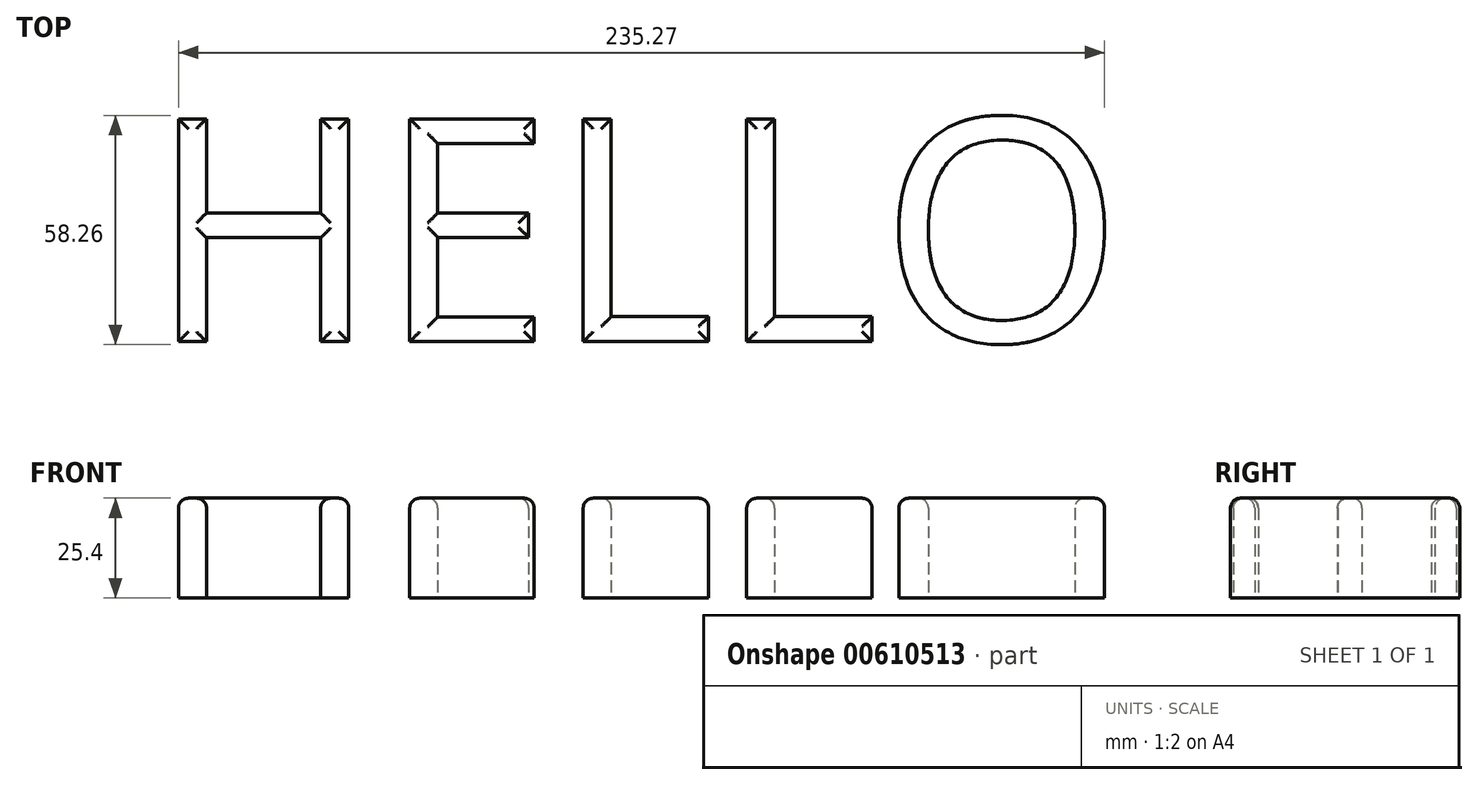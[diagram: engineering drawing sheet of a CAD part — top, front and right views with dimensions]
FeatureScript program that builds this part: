
annotation { "Feature Type Name" : "Feature", "Feature Type Description" : "" }
export const myFeature = defineFeature(function(context is Context, id is Id, definition is map)
    precondition{}
    {
        {
            var Q0;
            Q0=qCreatedBy(makeId("Top.planeOp"),FACE);
            var sketch = newSketch(context, id + "F0", { "sketchPlane" : qUnion([Q0])});
            skText(sketch, "E0", { "text": "HELLO", "fontName": "NotoSans-Regular.ttf"});
            const initialGuessF0  = {"E0": [-0.05312, -0.03037, 1, 0, 0.05707]};
            skSetInitialGuess(sketch, initialGuessF0);
            skSolve(sketch);
        }
        {
            var Q0;
            Q0 = qSketchRegion(id + "F0", true);
            extrude(context, id + "F1", {"entities" : qUnion([Q0]), "depth" : 25.4 * mm, "offsetDistance" : 25.4 * mm});
        }
        {
            var Q0;
            Q0=makeQuery(id+"F1.opExtrude","CAP_FACE",FACE,{"disambiguationData":[OSD([sQuery(id+"F0.wireOp",EDGE,"E0.sketch_text.stroke-0"),sQuery(id+"F0.wireOp",EDGE,"E0.sketch_text.stroke-1"),sQuery(id+"F0.wireOp",EDGE,"E0.sketch_text.stroke-2"),sQuery(id+"F0.wireOp",EDGE,"E0.sketch_text.stroke-3"),sQuery(id+"F0.wireOp",EDGE,"E0.sketch_text.stroke-4"),sQuery(id+"F0.wireOp",EDGE,"E0.sketch_text.stroke-5"),sQuery(id+"F0.wireOp",EDGE,"E0.sketch_text.stroke-6"),sQuery(id+"F0.wireOp",EDGE,"E0.sketch_text.stroke-7"),sQuery(id+"F0.wireOp",EDGE,"E0.sketch_text.stroke-8"),sQuery(id+"F0.wireOp",EDGE,"E0.sketch_text.stroke-9"),sQuery(id+"F0.wireOp",EDGE,"E0.sketch_text.stroke-10"),sQuery(id+"F0.wireOp",EDGE,"E0.sketch_text.stroke-11")])],"isStart":false});
            var Q1;
            Q1=makeQuery(id+"F1.opExtrude","CAP_FACE",FACE,{"disambiguationData":[OSD([sQuery(id+"F0.wireOp",EDGE,"E0.sketch_text.stroke-12"),sQuery(id+"F0.wireOp",EDGE,"E0.sketch_text.stroke-13"),sQuery(id+"F0.wireOp",EDGE,"E0.sketch_text.stroke-14"),sQuery(id+"F0.wireOp",EDGE,"E0.sketch_text.stroke-15"),sQuery(id+"F0.wireOp",EDGE,"E0.sketch_text.stroke-16"),sQuery(id+"F0.wireOp",EDGE,"E0.sketch_text.stroke-17"),sQuery(id+"F0.wireOp",EDGE,"E0.sketch_text.stroke-18"),sQuery(id+"F0.wireOp",EDGE,"E0.sketch_text.stroke-19"),sQuery(id+"F0.wireOp",EDGE,"E0.sketch_text.stroke-20"),sQuery(id+"F0.wireOp",EDGE,"E0.sketch_text.stroke-21"),sQuery(id+"F0.wireOp",EDGE,"E0.sketch_text.stroke-22"),sQuery(id+"F0.wireOp",EDGE,"E0.sketch_text.stroke-23")])],"isStart":false});
            var Q2;
            Q2=makeQuery(id+"F1.opExtrude","CAP_FACE",FACE,{"disambiguationData":[OSD([sQuery(id+"F0.wireOp",EDGE,"E0.sketch_text.stroke-24"),sQuery(id+"F0.wireOp",EDGE,"E0.sketch_text.stroke-25"),sQuery(id+"F0.wireOp",EDGE,"E0.sketch_text.stroke-26"),sQuery(id+"F0.wireOp",EDGE,"E0.sketch_text.stroke-27"),sQuery(id+"F0.wireOp",EDGE,"E0.sketch_text.stroke-28"),sQuery(id+"F0.wireOp",EDGE,"E0.sketch_text.stroke-29")])],"isStart":false});
            var Q3;
            Q3=makeQuery(id+"F1.opExtrude","CAP_FACE",FACE,{"disambiguationData":[OSD([sQuery(id+"F0.wireOp",EDGE,"E0.sketch_text.stroke-30"),sQuery(id+"F0.wireOp",EDGE,"E0.sketch_text.stroke-31"),sQuery(id+"F0.wireOp",EDGE,"E0.sketch_text.stroke-32"),sQuery(id+"F0.wireOp",EDGE,"E0.sketch_text.stroke-33"),sQuery(id+"F0.wireOp",EDGE,"E0.sketch_text.stroke-34"),sQuery(id+"F0.wireOp",EDGE,"E0.sketch_text.stroke-35")])],"isStart":false});
            var Q4;
            Q4=makeQuery(id+"F1.opExtrude","CAP_EDGE",EDGE,{"disambiguationData":[OSD([sQuery(id+"F0.wireOp",EDGE,"E0.sketch_text.stroke-45")])],"isStart":false});
            var Q5;
            Q5=makeQuery(id+"F1.opExtrude","CAP_EDGE",EDGE,{"disambiguationData":[OSD([sQuery(id+"F0.wireOp",EDGE,"E0.sketch_text.stroke-38")])],"isStart":false});
            fillet(context, id + "F2", {"entities" : qUnion([Q0, Q1, Q2, Q3, Q4, Q5]), "radius" : 2.54 * mm, "tangentPropagation" : true, "allowEdgeOverflow" : false});
        }
    });
